# Revit family: PRD_FrankeWS_ShwrFttngsPckg_WallArm_ZFAID0001
name_source: partatom
category: Plumbing Fixtures
revit_build: Autodesk Revit 2018 (Build: 20190510_1515(x64)
units: mm (PartAtom-declared; Revit-internal decimal feet)

## family parameters
Cut with Voids When Loaded = Yes
Host = Face
OmniClass Number = 23.45.05.14.99
OmniClass Title = Other Sanitary Washing Plumbing Fixtures
Part Type = Normal
Room Calculation Point = No
Round Connector Dimension = Use Diameter
Shared = Yes

## types (1)
- ZFAID0001
    AssetType = Fixed
    BIMObjectName = PRD_AR_ShowerFittingsPackage_WallArm_ZFAID0001
    Category = Pr_40_20_87_75, Shower fittings package
    Color = green
    Default Elevation = 925 mm  [stored 3.03478 ft]
    Description = Wall bracket with rosette for emergency shower head DN 20, green EPS coated brass (RAL 6032).
    DiameterNominal = 20  [stored 0.0656168 ft]
    DurationUnit = year
    Features = wall bracket with rosette for emergency shower head
    Finish = EPS coated
    FittingLossFactor = 0
    FittingMaterial = PRD_AR_Brass_EPSCoated_Green
    GrossWeight = 0.60 kg
    IfcExportAs = IfcPipeFittingType
    IfcExportType = USERDEFINED
    Manufacturer = KWC Group AG
    ManufacturerName = KWC Group AG
    ManufacturerURL = www.kwc.com
    Material = brass
    Model = ZFAID0001
    ModelNumber = 2030018827
    ModelReference = ZFAID0001
    NBSDescription = Shower fittings package
    NBSReference = 45-35-70/330
    Name = Wall Arm ZFAID0001
    NetWeight = 0.55 kg
    NominalDepth = 414 mm  [stored 1.35827 ft]
    NominalHeight = 93 mm  [stored 0.305118 ft]
    NominalWidth = 55 mm  [stored 0.180446 ft]
    PressureClass = 0.0 Pa
    PressureRange = 0.0 Pa
    ProductInformation = https://pim.kwc.com
    Size = 55 x 93 x 414 mm (W x H x D)
    Status = New
    TemperatureRange = 0 °C
    URL = www.kwc.com
    Uniclass2015Code = Pr_40_20_87_75
    Uniclass2015Title = Shower fittings package
    Uniclass2015Version = Products v1.17
    Version = 1
    WarrantyDurationUnit = year

note: [stored X ft] marks values corroborated as IEEE doubles in the binary element streams (Revit-internal decimal feet)

## geometry (parser evidence)
native form markers: Sweep x2
no freeform markers — native parametric forms only
